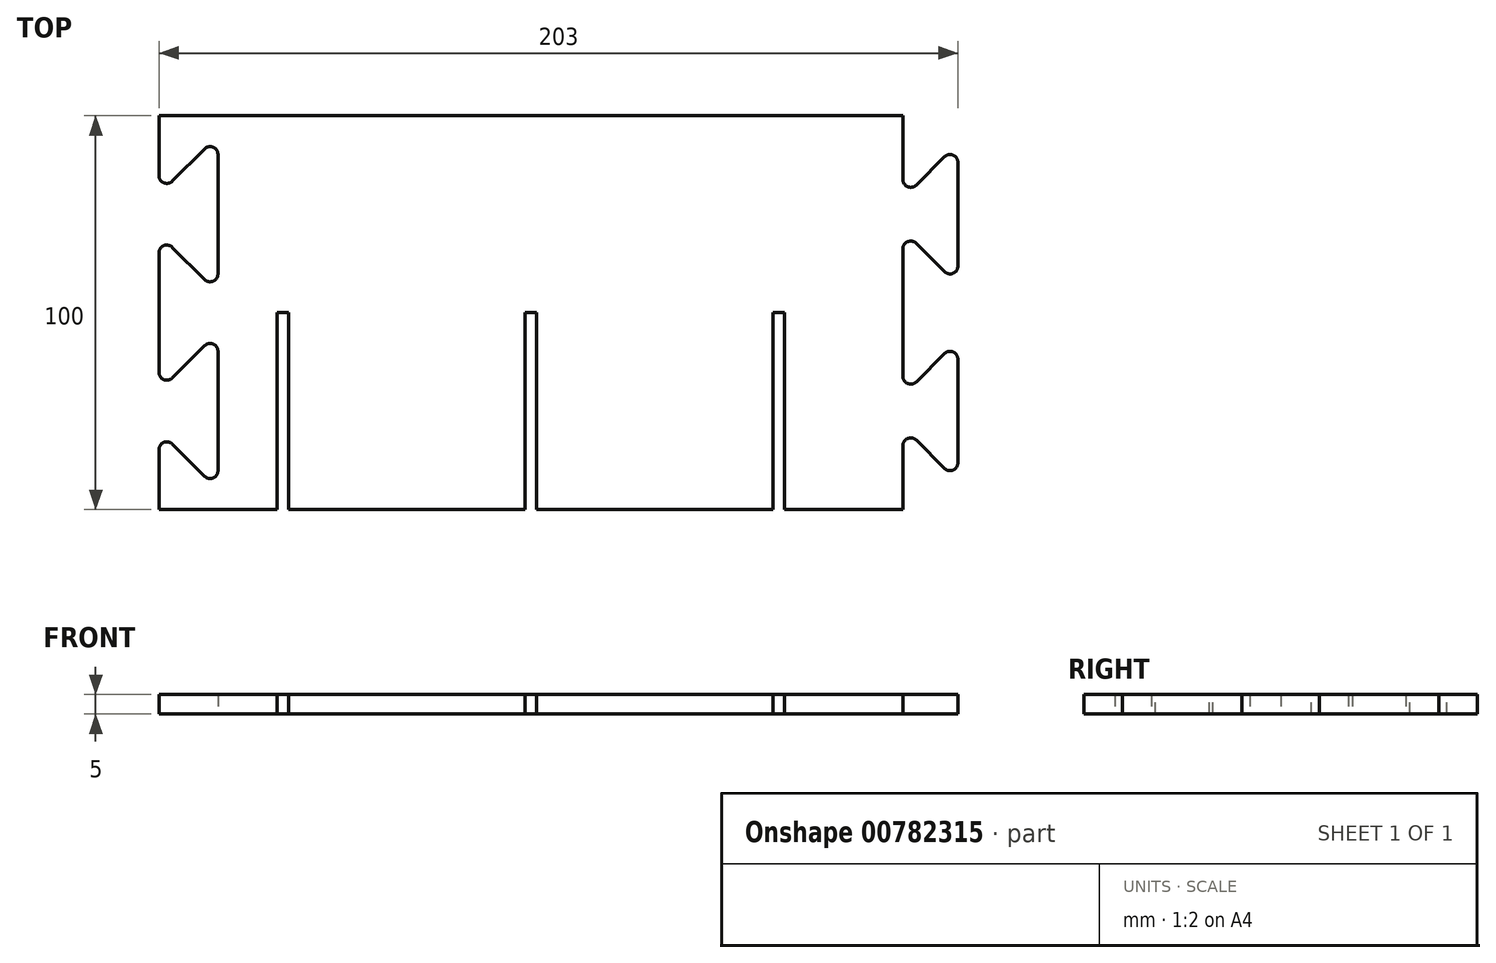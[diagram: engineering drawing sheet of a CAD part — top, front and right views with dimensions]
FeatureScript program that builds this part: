
annotation { "Feature Type Name" : "Feature", "Feature Type Description" : "" }
export const myFeature = defineFeature(function(context is Context, id is Id, definition is map)
    precondition{}
    {
        {
            var Q0;
            Q0=qCreatedBy(makeId("Top.planeOp"),FACE);
            var sketch = newSketch(context, id + "F0", { "sketchPlane" : qUnion([Q0])});
            skLineSegment(sketch, "E0.bottom", {"start": v(69, 50) * mm, "end": v(-120, 50) * mm});
            skLineSegment(sketch, "E0.top", {"start": v(99, -50) * mm, "end": v(39, -50) * mm});
            skLineSegment(sketch, "E0.right", {"start": v(-120, 50) * mm, "end": v(-120, 30) * mm});
            skPoint(sketch, "E0.middle", {"position": v(0, 0) * mm});
            skLineSegment(sketch, "E1", {"start": v(-120, -50) * mm, "end": v(-90, -50) * mm});
            skLineSegment(sketch, "E2.top", {"start": v(-90, 0) * mm, "end": v(-87, 0) * mm});
            skLineSegment(sketch, "E2.left", {"start": v(-90, -50) * mm, "end": v(-90, 0) * mm});
            skLineSegment(sketch, "E2.right", {"start": v(-87, -50) * mm, "end": v(-87, 0) * mm});
            skLineSegment(sketch, "E3", {"start": v(-87, -50) * mm, "end": v(-27, -50) * mm});
            skLineSegment(sketch, "E4.top", {"start": v(-27, 0) * mm, "end": v(-24, 0) * mm});
            skLineSegment(sketch, "E4.left", {"start": v(-27, -50) * mm, "end": v(-27, 0) * mm});
            skLineSegment(sketch, "E4.right", {"start": v(-24, -50) * mm, "end": v(-24, 0) * mm});
            skLineSegment(sketch, "E5", {"start": v(-24, -50) * mm, "end": v(36, -50) * mm});
            skLineSegment(sketch, "E6.top", {"start": v(36, 0) * mm, "end": v(39, 0) * mm});
            skLineSegment(sketch, "E6.left", {"start": v(36, -50) * mm, "end": v(36, 0) * mm});
            skLineSegment(sketch, "E6.right", {"start": v(39, -50) * mm, "end": v(39, 0) * mm});
            skLineSegment(sketch, "E7", {"start": v(39, -50) * mm, "end": v(69, -50) * mm});
            skLineSegment(sketch, "E8", {"start": v(69, -50) * mm, "end": v(69, -30) * mm});
            skPoint(sketch, "E0.left.start.orphan", {"position": v(120, 50) * mm});
            skPoint(sketch, "E9.orphan", {"position": v(120, -50) * mm});
            skLineSegment(sketch, "E10.trimOffspring", {"start": v(36, -50) * mm, "end": v(-24, -50) * mm});
            skLineSegment(sketch, "E11.trimOffspring", {"start": v(-27, -50) * mm, "end": v(-87, -50) * mm});
            skLineSegment(sketch, "E12.trimOffspring", {"start": v(-90, -50) * mm, "end": v(-120, -50) * mm});
            skLineSegment(sketch, "E13", {"start": v(-120, 0) * mm, "end": v(-120, 20) * mm});
            skLineSegment(sketch, "E14", {"start": v(-105, -25) * mm, "end": v(-105, -5) * mm});
            skLineSegment(sketch, "E15", {"start": v(-105, -25) * mm, "end": v(-105, -45) * mm});
            skLineSegment(sketch, "E16", {"start": v(-120, -20) * mm, "end": v(-105, -5) * mm});
            skLineSegment(sketch, "E17", {"start": v(-105, -45) * mm, "end": v(-120, -30) * mm});
            skLineSegment(sketch, "E18.trimOffspring", {"start": v(-120, -30) * mm, "end": v(-120, -50) * mm});
            skPoint(sketch, "E19.orphan", {"position": v(-120, -25) * mm});
            skLineSegment(sketch, "E20.MirrorCS", {"start": v(-120, 20) * mm, "end": v(-105, 5) * mm});
            skLineSegment(sketch, "E21.MirrorCS", {"start": v(-105, 25) * mm, "end": v(-105, 5) * mm});
            skLineSegment(sketch, "E22.MirrorCS", {"start": v(-105, 25) * mm, "end": v(-105, 45) * mm});
            skLineSegment(sketch, "E23.MirrorCS", {"start": v(-105, 45) * mm, "end": v(-120, 30) * mm});
            skLineSegment(sketch, "E24.trimOffspring", {"start": v(-120, 30) * mm, "end": v(-120, 50) * mm});
            skLineSegment(sketch, "E25.trimOffspring", {"start": v(-120, 20) * mm, "end": v(-120, -20) * mm});
            skLineSegment(sketch, "E26", {"start": v(84, 45) * mm, "end": v(84, 44) * mm});
            skLineSegment(sketch, "E27.trimOffspring", {"start": v(69, 30) * mm, "end": v(69, 50) * mm});
            skLineSegment(sketch, "E28.trimOffspring", {"start": v(69, -20) * mm, "end": v(69, 20) * mm});
            skLineSegment(sketch, "E29", {"start": v(69, 20) * mm, "end": v(69, 21) * mm});
            skLineSegment(sketch, "E30", {"start": v(69, 21) * mm, "end": v(83, 7) * mm});
            skLineSegment(sketch, "E31", {"start": v(83, 7) * mm, "end": v(83, 44) * mm});
            skLineSegment(sketch, "E32", {"start": v(83, 25) * mm, "end": v(67.34, 25) * mm});
            skLineSegment(sketch, "E33.MirrorCS", {"start": v(69, 29) * mm, "end": v(83, 43) * mm});
            skLineSegment(sketch, "E34.MirrorCS", {"start": v(83, 43) * mm, "end": v(83, 7) * mm});
            skPoint(sketch, "E35.trimOffspring.end.orphan", {"position": v(83, 4.47) * mm});
            skPoint(sketch, "E35.trimOffspring.start.orphan", {"position": v(83, 6) * mm});
            skPoint(sketch, "E36.orphan", {"position": v(84, 5) * mm});
            skPoint(sketch, "E37.orphan", {"position": v(84, 6) * mm});
            skLineSegment(sketch, "E38", {"start": v(69, 29) * mm, "end": v(69, 30) * mm});
            skPoint(sketch, "E39.orphan", {"position": v(84, 45) * mm});
            skPoint(sketch, "E40.orphan", {"position": v(83, 45.53) * mm});
            skPoint(sketch, "E41.orphan", {"position": v(83, 44) * mm});
            skLineSegment(sketch, "E42", {"start": v(69, -20) * mm, "end": v(69, -21) * mm});
            skPoint(sketch, "E43.MirrorCS.end.orphan", {"position": v(84, -5) * mm});
            skPoint(sketch, "E44.MirrorCS.start.orphan", {"position": v(84, -45) * mm});
            skLineSegment(sketch, "E45", {"start": v(69, 0) * mm, "end": v(97.29, 0) * mm});
            skLineSegment(sketch, "E46.MirrorCS", {"start": v(69, -21) * mm, "end": v(83, -7) * mm});
            skLineSegment(sketch, "E47.MirrorCS", {"start": v(83, -7) * mm, "end": v(83, -44) * mm});
            skLineSegment(sketch, "E48.MirrorCS", {"start": v(69, -29) * mm, "end": v(83, -43) * mm});
            skLineSegment(sketch, "E49.trimOffspring", {"start": v(69, -29) * mm, "end": v(69, -30) * mm});
            skSolve(sketch);
        }
        {
            var Q0;
            Q0=makeQuery(id+"F0.imprint","IMPRINT",FACE,{"disambiguationData":[TD([[makeQuery(id+"F0.imprint","IMPRINT",EDGE,{"derivedFrom":sQuery(id+"F0.wireOp",EDGE,"E0.bottom")}),1.0]])]});
            extrude(context, id + "F1", {"entities" : qUnion([Q0]), "depth" : 5 * mm, "offsetDistance" : 25.4 * mm});
        }
        {
            var Q0;
            Q0=makeQuery(id+"F1.opExtrude","SWEPT_EDGE",EDGE,{"disambiguationData":[OSD([sQuery(id+"F0.wireOp",EDGE,"E22.MirrorCS"),sQuery(id+"F0.wireOp",EDGE,"E23.MirrorCS")])]});
            var Q1;
            Q1=makeQuery(id+"F1.opExtrude","SWEPT_EDGE",EDGE,{"disambiguationData":[OSD([sQuery(id+"F0.wireOp",EDGE,"E20.MirrorCS"),sQuery(id+"F0.wireOp",EDGE,"E21.MirrorCS")])]});
            var Q2;
            Q2=makeQuery(id+"F1.opExtrude","SWEPT_EDGE",EDGE,{"disambiguationData":[OSD([sQuery(id+"F0.wireOp",EDGE,"E14"),sQuery(id+"F0.wireOp",EDGE,"E16")])]});
            var Q3;
            Q3=makeQuery(id+"F1.opExtrude","SWEPT_EDGE",EDGE,{"disambiguationData":[OSD([sQuery(id+"F0.wireOp",EDGE,"E15"),sQuery(id+"F0.wireOp",EDGE,"E17")])]});
            var Q4;
            Q4=makeQuery(id+"F1.opExtrude","SWEPT_EDGE",EDGE,{"disambiguationData":[OSD([sQuery(id+"F0.wireOp",EDGE,"E16"),sQuery(id+"F0.wireOp",EDGE,"E25.trimOffspring")])]});
            var Q5;
            Q5=makeQuery(id+"F1.opExtrude","SWEPT_EDGE",EDGE,{"disambiguationData":[OSD([sQuery(id+"F0.wireOp",EDGE,"E17"),sQuery(id+"F0.wireOp",EDGE,"E18.trimOffspring")])]});
            var Q6;
            Q6=makeQuery(id+"F1.opExtrude","SWEPT_EDGE",EDGE,{"disambiguationData":[OSD([sQuery(id+"F0.wireOp",EDGE,"E20.MirrorCS"),sQuery(id+"F0.wireOp",EDGE,"E25.trimOffspring")])]});
            var Q7;
            Q7=makeQuery(id+"F1.opExtrude","SWEPT_EDGE",EDGE,{"disambiguationData":[OSD([sQuery(id+"F0.wireOp",EDGE,"E23.MirrorCS"),sQuery(id+"F0.wireOp",EDGE,"E24.trimOffspring")])]});
            fillet(context, id + "F2", {"entities" : qUnion([Q0, Q1, Q2, Q3, Q4, Q5, Q6, Q7]), "radius" : 2 * mm, "tangentPropagation" : true, "allowEdgeOverflow" : false});
        }
        {
            var Q0;
            Q0=makeQuery(id+"F1.opExtrude","SWEPT_EDGE",EDGE,{"disambiguationData":[OSD([sQuery(id+"F0.wireOp",EDGE,"E33.MirrorCS"),sQuery(id+"F0.wireOp",EDGE,"E34.MirrorCS")])]});
            var Q1;
            Q1=makeQuery(id+"F1.opExtrude","SWEPT_EDGE",EDGE,{"disambiguationData":[OSD([sQuery(id+"F0.wireOp",EDGE,"E30"),sQuery(id+"F0.wireOp",EDGE,"E34.MirrorCS")])]});
            var Q2;
            Q2=makeQuery(id+"F1.opExtrude","SWEPT_EDGE",EDGE,{"disambiguationData":[OSD([sQuery(id+"F0.wireOp",EDGE,"E46.MirrorCS"),sQuery(id+"F0.wireOp",EDGE,"E47.MirrorCS")])]});
            var Q3;
            Q3=makeQuery(id+"F1.opExtrude","SWEPT_EDGE",EDGE,{"disambiguationData":[OSD([sQuery(id+"F0.wireOp",EDGE,"E47.MirrorCS"),sQuery(id+"F0.wireOp",EDGE,"E48.MirrorCS")])]});
            fillet(context, id + "F3", {"entities" : qUnion([Q0, Q1, Q2, Q3]), "radius" : 2 * mm, "tangentPropagation" : true, "allowEdgeOverflow" : false});
        }
        {
            var Q0;
            Q0=makeQuery(id+"F1.opExtrude","SWEPT_EDGE",EDGE,{"disambiguationData":[OSD([sQuery(id+"F0.wireOp",EDGE,"E29"),sQuery(id+"F0.wireOp",EDGE,"E30")])]});
            var Q1;
            Q1=makeQuery(id+"F1.opExtrude","SWEPT_EDGE",EDGE,{"disambiguationData":[OSD([sQuery(id+"F0.wireOp",EDGE,"E33.MirrorCS"),sQuery(id+"F0.wireOp",EDGE,"E38")])]});
            var Q2;
            Q2=makeQuery(id+"F1.opExtrude","SWEPT_EDGE",EDGE,{"disambiguationData":[OSD([sQuery(id+"F0.wireOp",EDGE,"E42"),sQuery(id+"F0.wireOp",EDGE,"E46.MirrorCS")])]});
            var Q3;
            Q3=makeQuery(id+"F1.opExtrude","SWEPT_EDGE",EDGE,{"disambiguationData":[OSD([sQuery(id+"F0.wireOp",EDGE,"E48.MirrorCS"),sQuery(id+"F0.wireOp",EDGE,"E49.trimOffspring")])]});
            fillet(context, id + "F4", {"entities" : qUnion([Q0, Q1, Q2, Q3]), "radius" : 2 * mm, "tangentPropagation" : true, "allowEdgeOverflow" : false});
        }
    });
